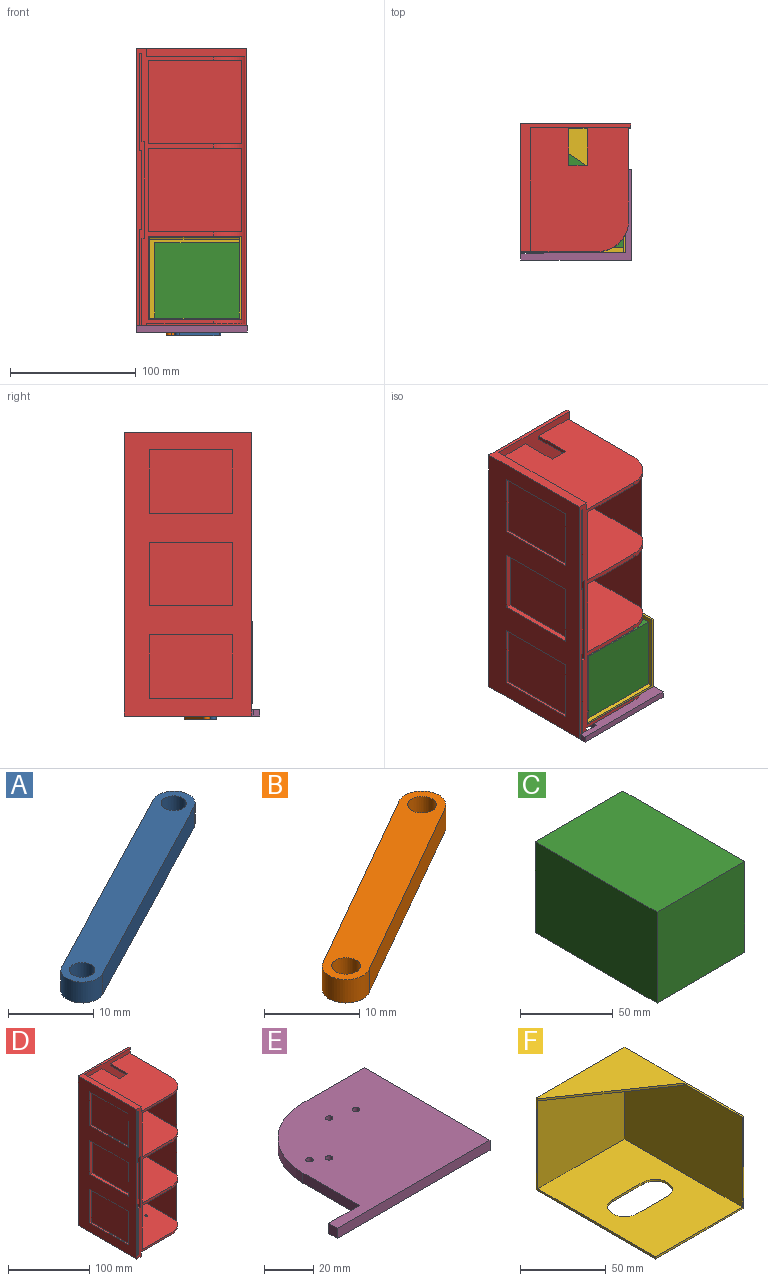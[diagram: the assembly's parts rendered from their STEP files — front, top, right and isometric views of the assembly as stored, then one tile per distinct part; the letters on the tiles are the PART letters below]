
ASSEMBLY  parts=6 mates=12
PART A: 8 faces, bbox 36.6x21.4x3 mm
  f0: cylinder r=2.5mm len=4.72mm, axis (0,0,1), area 23.6mm2, adj f1,f4,f6,f7
  f1: plane 31.6x16.38mm, normal (-0.46,0.89,0), area 106.8mm2, adj f0,f2,f6,f7
  f2: cylinder r=2.5mm len=4.72mm, axis (0,0,1), area 23.6mm2, adj f1,f4,f6,f7
  f3: cylinder r=1.5mm len=3mm, axis (0,0,1), area 28.3mm2, adj f6,f7
  f4: plane 31.6x16.38mm, normal (0.46,-0.89,0), area 106.8mm2, adj f0,f2,f6,f7
  f5: cylinder r=1.5mm len=3mm, axis (0,0,1), area 28.3mm2, adj f6,f7
  f6: plane 36.6x21.38mm, normal (0,0,-1), area 183.5mm2, adj f0,f1,f2,f3,f4,f5
  f7: plane 36.6x21.38mm, normal (0,0,1), area 183.5mm2, adj f0,f1,f2,f3,f4,f5
PART B: 8 faces, bbox 31.4x20.1x3 mm
  f0: cylinder r=2.5mm len=4.67mm, axis (0,0,1), area 23.6mm2, adj f1,f3,f6,f7
  f1: plane 26.36x15.08mm, normal (0.5,-0.87,0), area 91.1mm2, adj f0,f2,f6,f7
  f2: cylinder r=2.5mm len=4.67mm, axis (0,0,1), area 23.6mm2, adj f1,f3,f6,f7
  f3: plane 26.36x15.08mm, normal (-0.5,0.87,0), area 91.1mm2, adj f0,f2,f6,f7
  f4: cylinder r=1.5mm len=3mm, axis (0,0,1), area 28.3mm2, adj f6,f7
  f5: cylinder r=1.5mm len=3mm, axis (0,0,1), area 28.3mm2, adj f6,f7
  f6: plane 31.36x20.08mm, normal (0,0,-1), area 157.3mm2, adj f0,f1,f2,f3,f4,f5
  f7: plane 31.36x20.08mm, normal (0,0,1), area 157.3mm2, adj f0,f1,f2,f3,f4,f5
PART C: 6 faces, bbox 67x93x60 mm
  f0: plane 67x60mm, normal (0,-1,0), area 4020mm2, adj f1,f3,f4,f5
  f1: plane 93x60mm, normal (1,0,0), area 5580mm2, adj f0,f2,f4,f5
  f2: plane 67x60mm, normal (0,1,0), area 4020mm2, adj f1,f3,f4,f5
  f3: plane 93x60mm, normal (-1,0,0), area 5580mm2, adj f0,f2,f4,f5
  f4: plane 93x67mm, normal (0,0,1), area 6231mm2, adj f0,f1,f2,f3
  f5: plane 93x67mm, normal (0,0,-1), area 6231mm2, adj f0,f1,f2,f3
PART D: 66 faces, bbox 87.5x101.5x225.5 mm
  f0: plane 225.5x101.5mm, normal (-1,0,0), area 12813.5mm2, adj f4,f16,f18,f19,f38,f39,f40,f41
  f1: plane 98.5x77mm, normal (1,0,0), area 4226.3mm2, adj f4,f26,f27,f36,f46,f47,f48,f49
  f2: plane 98.5x63mm, normal (1,0,0), area 2847.3mm2, adj f4,f27,f28,f36,f42,f43,f44,f45
  f3: plane 98.5x77mm, normal (1,0,0), area 4226.3mm2, adj f4,f28,f29,f36,f38,f39,f40,f41
  f4: plane 225.5x60.9mm, normal (0,-1,0), area 2369.1mm2, adj f0,f1,f2,f3,f6,f7,f8,f9
  f5: plane 85.37x66.3mm, normal (-1,0,0), area 5660.3mm2, adj f6,f15,f35,f37
  f6: plane 98.5x73.3mm, normal (0,0,1), area 6658.6mm2, adj f4,f5,f20,f35,f37,f59,f60,f61
  f7: plane 98.5x77.9mm, normal (0,0,-1), area 7060.7mm2, adj f4,f21,f22,f35,f37,f59,f60,f61
  f8: plane 98.5x77.9mm, normal (0,0,1), area 7089mm2, adj f4,f22,f23,f35,f37,f56,f57,f58
  f9: plane 98.5x73.3mm, normal (0,0,-1), area 6686.9mm2, adj f4,f10,f33,f35,f37,f56,f57,f58
  f10: plane 85.37x66.3mm, normal (-1,0,0), area 5660.3mm2, adj f9,f11,f35,f37
  f11: plane 98.5x73.3mm, normal (0,0,1), area 6686.9mm2, adj f4,f10,f33,f35,f37,f53,f54,f55
  f12: plane 98.5x73.3mm, normal (0,0,-1), area 6686.9mm2, adj f4,f13,f34,f35,f37,f53,f54,f55
  f13: plane 85.37x66.3mm, normal (-1,0,0), area 5660.3mm2, adj f12,f14,f35,f37
  f14: plane 98.5x73.3mm, normal (0,0,1), area 6686.9mm2, adj f4,f13,f34,f35,f37,f50,f51,f52
  f15: plane 98.5x73.3mm, normal (0,0,-1), area 6686.9mm2, adj f4,f5,f20,f35,f37,f50,f51,f52
  f16: plane 101.5x87.5mm, normal (0,0,1), area 1050.5mm2, adj f0,f4,f17,f19,f23,f35
  f17: plane 225.5x3mm, normal (1,0,0), area 676.5mm2, adj f16,f18,f19,f35
  f18: plane 101.5x87.5mm, normal (0,0,-1), area 1050.5mm2, adj f0,f4,f17,f19,f21,f35
  f19: plane 225.5x87.5mm, normal (0,1,0), area 19731.2mm2, adj f0,f16,f17,f18
  f20: plane 98.5x66.3mm, normal (1,0,0), area 6530.6mm2, adj f4,f6,f15,f35
  f21: plane 98.5x6.6mm, normal (1,0,0), area 650.1mm2, adj f4,f7,f18,f35
  f22: plane 212.3x73.5mm, normal (1,0,0), area 15604.1mm2, adj f7,f8,f35,f37
  f23: plane 98.5x6.6mm, normal (1,0,0), area 650.1mm2, adj f4,f8,f16,f35
  f24: plane 98.5x2mm, normal (0,0,1), area 197mm2, adj f4,f25,f32,f36
  f25: plane 98.5x70mm, normal (-1,0,0), area 6895mm2, adj f4,f24,f26,f36
  f26: plane 98.5x2mm, normal (0,0,1), area 197mm2, adj f1,f4,f25,f36
  f27: plane 98.5x2mm, normal (0,0,-1), area 197mm2, adj f1,f2,f4,f36
  f28: plane 98.5x2mm, normal (0,0,1), area 197mm2, adj f2,f3,f4,f36
  f29: plane 98.5x2mm, normal (0,0,-1), area 197mm2, adj f3,f4,f30,f36
  f30: plane 98.5x70mm, normal (-1,0,0), area 6895mm2, adj f4,f29,f31,f36
  f31: plane 98.5x2mm, normal (0,0,-1), area 197mm2, adj f4,f30,f32,f36
  f32: plane 98.5x77mm, normal (-1,0,0), area 7584.5mm2, adj f4,f24,f31,f36
  f33: plane 98.5x66.3mm, normal (1,0,0), area 6530.6mm2, adj f4,f9,f11,f35
  f34: plane 98.5x66.3mm, normal (1,0,0), area 6530.6mm2, adj f4,f12,f14,f35
  f35: plane 225.5x79.5mm, normal (0,-1,0), area 16169.5mm2, adj f5,f6,f7,f8,f9,f10,f11,f12
  f36: plane 217x4mm, normal (0,-1,0), area 462mm2, adj f1,f2,f3,f24,f25,f26,f27,f28
  f37: cylinder r=25mm len=212.3mm, axis (0,0,-1), area 2987.3mm2, adj f4,f5,f6,f7,f8,f9,f10,f11
  f38: plane 66.5x2mm, normal (0,0,1), area 133mm2, adj f0,f3,f39,f41
  f39: plane 50.5x2mm, normal (0,1,0), area 101mm2, adj f0,f3,f38,f40
  f40: plane 66.5x2mm, normal (0,0,-1), area 133mm2, adj f0,f3,f39,f41
  f41: plane 50.5x2mm, normal (0,-1,0), area 101mm2, adj f0,f3,f38,f40
  f42: plane 66.5x4mm, normal (0,0,1), area 266mm2, adj f0,f2,f43,f45
  f43: plane 50.5x4mm, normal (0,1,0), area 202mm2, adj f0,f2,f42,f44
  f44: plane 66.5x4mm, normal (0,0,-1), area 266mm2, adj f0,f2,f43,f45
  f45: plane 50.5x4mm, normal (0,-1,0), area 202mm2, adj f0,f2,f42,f44
  f46: plane 66.5x2mm, normal (0,0,1), area 133mm2, adj f0,f1,f47,f49
  f47: plane 50.5x2mm, normal (0,1,0), area 101mm2, adj f0,f1,f46,f48
  f48: plane 66.5x2mm, normal (0,0,-1), area 133mm2, adj f0,f1,f47,f49
  f49: plane 50.5x2mm, normal (0,-1,0), area 101mm2, adj f0,f1,f46,f48
  f50: plane 15x3.7mm, normal (0,1,0), area 55.5mm2, adj f14,f15,f51,f52
  f51: plane 30x3.7mm, normal (-1,0,0), area 111mm2, adj f14,f15,f35,f50
  f52: plane 30x3.7mm, normal (1,0,0), area 111mm2, adj f14,f15,f35,f50
  f53: plane 15x3.7mm, normal (0,1,0), area 55.5mm2, adj f11,f12,f54,f55
  f54: plane 30x3.7mm, normal (-1,0,0), area 111mm2, adj f11,f12,f35,f53
  f55: plane 30x3.7mm, normal (1,0,0), area 111mm2, adj f11,f12,f35,f53
  f56: plane 15x3mm, normal (0,1,0), area 45mm2, adj f8,f9,f57,f58
  f57: plane 30x3mm, normal (-1,0,0), area 90mm2, adj f8,f9,f35,f56
  f58: plane 30x3mm, normal (1,0,0), area 90mm2, adj f8,f9,f35,f56
  f59: plane 15x3mm, normal (0,1,0), area 45mm2, adj f6,f7,f60,f61
  f60: plane 30x3mm, normal (1,0,0), area 90mm2, adj f6,f7,f35,f59
  f61: plane 30x3mm, normal (-1,0,0), area 90mm2, adj f6,f7,f35,f59
  f62: cylinder r=1.5mm len=3mm, axis (0,0,-1), area 28.3mm2, adj f6,f7
  f63: cylinder r=1.5mm len=3mm, axis (0,0,-1), area 28.3mm2, adj f6,f7
  f64: cylinder r=1.5mm len=3mm, axis (0,0,-1), area 28.3mm2, adj f6,f7
  f65: cylinder r=1.5mm len=3mm, axis (0,0,-1), area 28.3mm2, adj f6,f7
PART E: 13 faces, bbox 87.5x72.1x5 mm
  f0: plane 32.31x5mm, normal (-1,0,0), area 161.6mm2, adj f1,f6,f7,f8
  f1: cylinder r=34.8mm len=34.8mm, axis (0,0,-1), area 273.3mm2, adj f0,f2,f7,f8
  f2: plane 35.09x5mm, normal (0,1,0), area 175.4mm2, adj f1,f3,f7,f8
  f3: plane 72.11x5mm, normal (1,0,0), area 360.6mm2, adj f2,f4,f7,f8
  f4: plane 87.5x5mm, normal (0,-1,0), area 437.5mm2, adj f3,f5,f7,f8
  f5: plane 5x5mm, normal (-1,0,0), area 25mm2, adj f4,f6,f7,f8
  f6: plane 17.61x5mm, normal (0,1,0), area 88.1mm2, adj f0,f5,f7,f8
  f7: plane 87.5x72.11mm, normal (0,0,1), area 4839.6mm2, adj f0,f1,f2,f3,f4,f5,f6,f9
  f8: plane 87.5x72.11mm, normal (0,0,-1), area 4839.6mm2, adj f0,f1,f2,f3,f4,f5,f6,f9
  f9: cylinder r=1.5mm len=5mm, axis (0,0,-1), area 47.1mm2, adj f7,f8
  f10: cylinder r=1.5mm len=5mm, axis (0,0,-1), area 47.1mm2, adj f7,f8
  f11: cylinder r=1.5mm len=5mm, axis (0,0,-1), area 47.1mm2, adj f7,f8
  f12: cylinder r=1.5mm len=5mm, axis (0,0,-1), area 47.1mm2, adj f7,f8
PART F: 15 faces, bbox 72.5x98.5x65.5 mm
  f0: plane 98.5x72.5mm, normal (0,0,-1), area 6327.1mm2, adj f2,f3,f9,f10,f11,f12,f13,f14
  f1: plane 97x71mm, normal (0,0,1), area 6072.8mm2, adj f4,f5,f9,f10,f11,f12,f13,f14
  f2: plane 72.5x65.5mm, normal (0,1,0), area 4748.7mm2, adj f0,f3,f6,f10
  f3: plane 98.5x65.5mm, normal (1,0,0), area 6451.8mm2, adj f0,f2,f6,f9
  f4: plane 71x62.5mm, normal (0,-1,0), area 4437.5mm2, adj f1,f5,f8,f10
  f5: plane 97x64mm, normal (-1,0,0), area 6135.2mm2, adj f1,f4,f6,f7,f8,f9
  f6: plane 98.5x72.5mm, normal (0,0,1), area 1976mm2, adj f2,f3,f5,f7,f9,f10
  f7: plane 71x48.5mm, normal (-0.56,-0.83,0), area 129mm2, adj f5,f6,f8,f10
  f8: plane 71x48.5mm, normal (0,0,-1), area 1721.8mm2, adj f4,f5,f7
  f9: plane 72.5x65.5mm, normal (0,-1,0), area 204.8mm2, adj f0,f1,f3,f5,f6,f10
  f10: plane 98.5x65.5mm, normal (-1,0,0), area 243.8mm2, adj f0,f1,f2,f4,f6,f7,f9
  f11: cylinder r=10mm len=20mm, axis (0,0,-1), area 47.1mm2, adj f0,f1,f12,f14
  f12: plane 25x1.5mm, normal (0,-1,0), area 37.5mm2, adj f0,f1,f11,f13
  f13: cylinder r=10mm len=20mm, axis (0,0,-1), area 47.1mm2, adj f0,f1,f12,f14
  f14: plane 25x1.5mm, normal (0,1,0), area 37.5mm2, adj f0,f1,f11,f13
PLACE A rot(axis=(0,0,1),0.7deg) t=(-35.42,29.48,-21.13)mm
PLACE B rot(axis=(0,0,-1),0.9deg) t=(-35.22,29.4,-32.63)mm
PLACE C t=(-33.01,31.46,-21.53)mm
PLACE D t=(-35.41,29.71,-21.13)mm fixed
PLACE E rot(axis=(0,0,-1),0.1deg) t=(-35.18,29.31,-21.13)mm
PLACE F t=(-35.01,29.46,-21.53)mm
MATE planar F.f4 <-> C.f2  axis (0,-1,0) through (-35.01,77.96,9.72)mm
MATE cylindrical A.f0 <-> E.f9  axis (0,0,1) through (-48.09,12.14,-35.63)mm
MATE planar C.f1 <-> F.f5  axis (1,0,0) through (0.49,31.46,8.47)mm
MATE planar E.f8 <-> D.f18  axis (0,0,-1) through (-27.44,8.65,-32.63)mm
MATE planar F.f3 <-> D.f5  axis (1,0,0) through (1.99,30.21,9.72)mm
MATE cylindrical B.f0 <-> D.f63  axis (0,0,1) through (-54.85,17.24,-35.63)mm
MATE planar E.f8 <-> B.f7  axis (0,0,-1) through (6.73,-25.26,-32.63)mm
MATE cylindrical B.f2 <-> E.f12  axis (0,0,1) through (-28.26,31.91,-34.13)mm
MATE planar D.f6 <-> F.f0  axis (0,0,1) through (-45.66,-18.79,-23.03)mm
MATE planar C.f5 <-> F.f1  axis (0,0,-1) through (-33.01,31.46,-21.53)mm
MATE planar A.f7 <-> E.f8  axis (0,0,1) through (-32.39,20.52,-32.63)mm
MATE cylindrical A.f2 <-> D.f64  axis (0,0,1) through (-16.69,28.9,-35.63)mm
